# Revit family: TД_РАШВОРК_100-PN10
name_source: partatom
category: Арматура трубопроводов
units: mm (PartAtom-declared; Revit-internal decimal feet)

## family parameters
Всегда вертикально = Да
На основе рабочей плоскости = Нет
Общий = Нет
При загрузке вырезать с полостями = Нет
Размер круглого соединителя = Использовать диаметр
Тип детали = Нормальный

## types (8) — shared parameters
ADSK_Единица измерения = шт
ADSK_Завод-изготовитель = ООО ТД "РАШВОРК"
H2 = 60 мм
HH = 28 мм
L2 = 16 мм
URL = https://rwru.ru
Длина = 342 мм
Корпус = GGG40
zero-valued in all types: Отметка по умолчанию

## per-type parameters (varying)
| type | ADSK_Масса | ADSK_Наименование краткое | B | D | D1 | DN | DNсоединителя | G | H | H1 | L | L1 | V1 | f | Высота | Штурвал |
| Задвижка с обрезиненным клином РАШВОРК 100-200-10, DN200, PN10, корпус - GJS-500-7 (GGG50), клин - GJS-500-7 (GGG50), уплотнение - EPDM, Ф/Ф, штурвал | 52 | 100-200-10 | 20 мм | 340 мм | 110 мм | 200 мм | 200 мм | 266 мм | 492 мм | 409 мм | 230 мм | 150 мм | 310 мм | 3 мм | 115 мм | Штурвал : 340 |
| Задвижка с обрезиненным клином РАШВОРК 100-250-10, DN250, PN10, корпус - GJS-500-7 (GGG50), клин - GJS-500-7 (GGG50), уплотнение - EPDM, Ф/Ф, штурвал | 80 | 100-250-10 | 22 мм | 405 мм | 125 мм | 250 мм | 250 мм | 319 мм | 571 мм | 476 мм | 250 мм | 170 мм | 370 мм | 3 мм | 125 мм | Штурвал : 340 |
| Задвижка с обрезиненным клином РАШВОРК 100-300-10, DN300, PN10, корпус - GJS-500-7 (GGG50), клин - GJS-500-7 (GGG50), уплотнение - EPDM, Ф/Ф, штурвал | 110 | 100-300-10 | 25 мм | 460 мм | 164 мм | 300 мм | 300 мм | 370 мм | 663 мм | 544 мм | 270 мм | 170 мм | 410 мм | 4 мм | 135 мм | Штурвал : 400 |
| Задвижка с обрезиненным клином РАШВОРК 100-350-10, DN350, PN10, корпус - GJS-500-7 (GGG50), клин - GJS-500-7 (GGG50), уплотнение - EPDM, Ф/Ф, штурвал | 210 | 100-350-10 | 27 мм | 520 мм | 198 мм | 350 мм | 350 мм | 429 мм | 800 мм | 724 мм | 290 мм | 210 мм | 530 мм | 4 мм | 145 мм | Штурвал : 450 |
| Задвижка с обрезиненным клином РАШВОРК 100-400-10, DN400, PN10, корпус - GJS-500-7 (GGG50), клин - GJS-500-7 (GGG50), уплотнение - EPDM, Ф/Ф, штурвал | 269 | 100-400-10 | 28 мм | 580 мм | 220 мм | 400 мм | 400 мм | 480 мм | 880 мм | 762 мм | 310 мм | 210 мм | 595 мм | 4 мм | 155 мм | Штурвал : 450 |
| Задвижка с обрезиненным клином РАШВОРК 100-450-10, DN450, PN10, корпус - GJS-500-7 (GGG50), клин - GJS-500-7 (GGG50), уплотнение - EPDM, Ф/Ф, штурвал | 338 | 100-450-10 | 30 мм | 640 мм | 235 мм | 450 мм | 450 мм | 530 мм | 958 мм | 810 мм | 330 мм | 220 мм | 630 мм | 4 мм | 165 мм | Штурвал : 450 |
| Задвижка с обрезиненным клином РАШВОРК 100-500-10, DN500, PN10, корпус - GJS-500-7 (GGG50), клин - GJS-500-7 (GGG50), уплотнение - EPDM, Ф/Ф, штурвал | 442 | 100-500-10 | 32 мм | 715 мм | 275 мм | 500 мм | 500 мм | 582 мм | 1004 мм | 932 мм | 350 мм | 284 мм | 700 мм | 4 мм | 175 мм | Штурвал : 600 |
| Задвижка с обрезиненным клином РАШВОРК 100-600-10, DN600, PN10, корпус - GJS-500-7 (GGG50), клин - GJS-500-7 (GGG50), уплотнение - EPDM, Ф/Ф, штурвал | 524 | 100-600-10 | 36 мм | 840 мм | 300 мм | 600 мм | 600 мм | 682 мм | 1157 мм | 1052 мм | 390 мм | 312 мм | 775 мм | 5 мм | 195 мм | Штурвал : 600 |

note: column(s) folded — value = type name in every type: ADSK_Наименование

## geometry (parser evidence)
native form markers: Blend x4
no freeform markers — native parametric forms only
